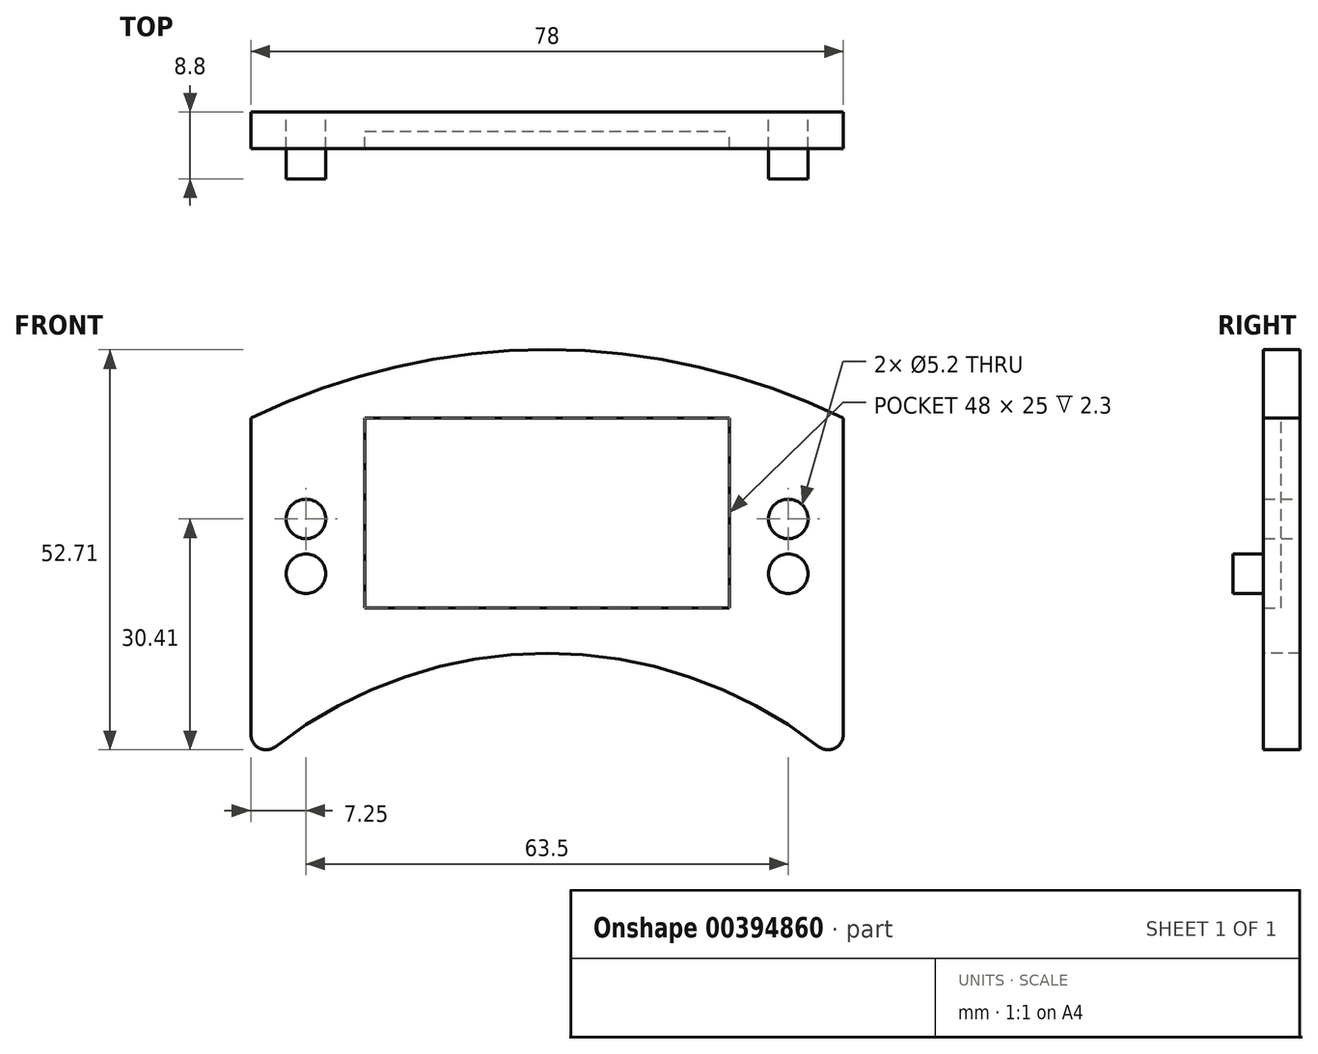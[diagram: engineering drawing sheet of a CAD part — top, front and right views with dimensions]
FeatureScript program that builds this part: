
annotation { "Feature Type Name" : "Feature", "Feature Type Description" : "" }
export const myFeature = defineFeature(function(context is Context, id is Id, definition is map)
    precondition{}
    {
        {
            var Q0;
            Q0=qCreatedBy(makeId("Front.planeOp"),FACE);
            var sketch = newSketch(context, id + "F0", { "sketchPlane" : qUnion([Q0])});
            skLineSegment(sketch, "E0", {"start": v(-39, -46) * mm, "end": v(-39, 0) * mm});
            skLineSegment(sketch, "E1", {"start": v(-39, 0) * mm, "end": v(39, 0) * mm, "construction": true});
            skLineSegment(sketch, "E2", {"start": v(39, 0) * mm, "end": v(39, -46) * mm});
            skArc(sketch, "E3", {"start": v(39, -46) * mm, "mid": v(0, -31) * mm, "end": v(-39, -46) * mm});
            skArc(sketch, "E4", {"start": v(39, 0) * mm, "mid": v(0, 9) * mm, "end": v(-39, 0) * mm});
            skSolve(sketch);
        }
        {
            var Q0;
            Q0=qSketchRegion(id+"F0",true);
            extrude(context, id + "F1", {"entities" : qUnion([Q0]), "oppositeDirection" : true, "depth" : 4.8 * mm});
        }
        {
            var Q0;
            Q0=makeQuery(id+"F1.opExtrude","CAP_FACE",FACE,{"disambiguationData":[OSD([sQuery(id+"F0.wireOp",EDGE,"E0"),sQuery(id+"F0.wireOp",EDGE,"E2"),sQuery(id+"F0.wireOp",EDGE,"E3"),sQuery(id+"F0.wireOp",EDGE,"E4")])],"isStart":true});
            var sketch = newSketch(context, id + "F2", { "sketchPlane" : qUnion([Q0])});
            skCircle(sketch, "E5", {"center": v(-31.75, -20.5) * mm, "radius": 2.6 * mm});
            skCircle(sketch, "E6", {"center": v(31.75, -20.5) * mm, "radius": 2.6 * mm});
            skSolve(sketch);
        }
        {
            var Q0;
            Q0 = qSketchRegion(id + "F2", true);
            extrude(context, id + "F3", {"entities" : qUnion([Q0]), "operationType" : NewBodyOperationType.ADD, "depth" : 4 * mm});
        }
        {
            var Q0;
            Q0=makeQuery(id+"F1.opExtrude","CAP_FACE",FACE,{"disambiguationData":[OSD([sQuery(id+"F0.wireOp",EDGE,"E0"),sQuery(id+"F0.wireOp",EDGE,"E2"),sQuery(id+"F0.wireOp",EDGE,"E3"),sQuery(id+"F0.wireOp",EDGE,"E4")])],"isStart":false});
            var sketch = newSketch(context, id + "F4", { "sketchPlane" : qUnion([Q0])});
            skPoint(sketch, "E7", {"position": v(-31.75, -20.5) * mm});
            skPoint(sketch, "E8", {"position": v(31.75, -20.5) * mm});
            skCircle(sketch, "E9", {"center": v(-31.75, -20.5) * mm, "radius": 2.6 * mm, "construction": true});
            skCircle(sketch, "E10", {"center": v(31.75, -20.5) * mm, "radius": 2.6 * mm, "construction": true});
            skCircle(sketch, "E11", {"center": v(-31.75, -13.3) * mm, "radius": 2.6 * mm});
            skCircle(sketch, "E12.MirrorC", {"center": v(31.75, -13.3) * mm, "radius": 2.6 * mm});
            skSolve(sketch);
        }
        {
            var Q0;
            Q0 = qSketchRegion(id + "F4", true);
            extrude(context, id + "F5", {"entities" : qUnion([Q0]), "operationType" : NewBodyOperationType.REMOVE, "endBound" : BoundingType.UP_TO_NEXT, "oppositeDirection" : true, "depth" : 2.2 * mm});
        }
        {
            var Q0;
            Q0=makeQuery(id+"F1.opExtrude","SWEPT_EDGE",EDGE,{"disambiguationData":[OSD([sQuery(id+"F0.wireOp",EDGE,"E0"),sQuery(id+"F0.wireOp",EDGE,"E3")])]});
            var Q1;
            Q1=makeQuery(id+"F1.opExtrude","SWEPT_EDGE",EDGE,{"disambiguationData":[OSD([sQuery(id+"F0.wireOp",EDGE,"E2"),sQuery(id+"F0.wireOp",EDGE,"E3")])]});
            fillet(context, id + "F6", {"entities" : qUnion([Q0, Q1]), "radius" : 2 * mm, "tangentPropagation" : true, "allowEdgeOverflow" : false});
        }
        {
            var Q0;
            Q0=qCreatedBy(makeId("Top.planeOp"),FACE);
            var sketch = newSketch(context, id + "F7", { "sketchPlane" : qUnion([Q0])});
            skLineSegment(sketch, "E13.bottom", {"start": v(-24, 0) * mm, "end": v(24, 0) * mm});
            skLineSegment(sketch, "E13.top", {"start": v(-24, 2.3) * mm, "end": v(24, 2.3) * mm});
            skLineSegment(sketch, "E13.left", {"start": v(-24, 0) * mm, "end": v(-24, 2.3) * mm});
            skLineSegment(sketch, "E13.right", {"start": v(24, 0) * mm, "end": v(24, 2.3) * mm});
            skSolve(sketch);
        }
        {
            var Q0;
            Q0 = qSketchRegion(id + "F7", true);
            extrude(context, id + "F8", {"entities" : qUnion([Q0]), "operationType" : NewBodyOperationType.REMOVE, "oppositeDirection" : true, "depth" : 25 * mm});
        }
    });
